# Revit family: Kessel 83091 en
name_source: partatom
category: Pipe Accessories
revit_build: Autodesk Revit Architecture 2014 (Build: 20130308_1515(x64)
units: mm (PartAtom-declared; Revit-internal decimal feet)

## types (1)
- Kessel 83091 en
    <1.010.00.2> Number of the part of the guideline = 38
    <1.010.00.3> Issue date (month) of the guideline = 201805
    <1.010.00.4> Manufacturer name = Kessel
    <1.010.00.5> Revision date of the file = 20190228
    <1.800.00.3> BS number = 1060010000000000000000000000000000000000000000002300000000
    <1.800.00.4> Comment field = Socket DN 90
    <1.810.00.3> Manufacturer’s reference number = 83091
    <1.810.00.4> DATANORM number = 83091
    <1.810.00.6> GTIN number = 4026092076934
    <1.960/3L.00.8> Link (URL) = http://www.kessel.de
    <38.100.00.4> Drain type for floor, roof and sanitary objects = Backwater valve accessories
    <38.110.00.4> Floor, roof and sanitary works sequences = Accessories
    <38.700.00.15> Connection to GLT, GA = no
    <38.700.00.16> Fire resistance class can be retrofitted = no
    <38.700.00.4> product name = Socket DN 90
    <38.700.00.6> Complete article (one-piece) from combination (multi-part design) Drain body and attachment piece = no
    <38.700.00.7> Potential compensation (ground connection) available = no
    <38.700.00.8> Electrical connection = no
    CONNECTOR0_DIAMETER_dZ_0r = 0 mm  [stored 0 ft]
    CONNECTOR0_dZ_00 = 15 mm
    CONNECTOR0_ref_dZ = 15 mm
    CONNECTOR1_DIAMETER_dZ_0r = 0 mm  [stored 0 ft]
    CONNECTOR1_dZ_00 = 83 mm
    CONNECTOR1_dZ_01 = 63 mm
    CONNECTOR1_ref_dX = 10 mm  [stored 0.0328084 ft]
    CONNECTOR1_ref_dZ = 63 mm
    Manufacturer = Kessel
    Model = 83091
    URL = www.kessel.com

note: [stored X ft] marks values corroborated as IEEE doubles in the binary element streams (Revit-internal decimal feet)
